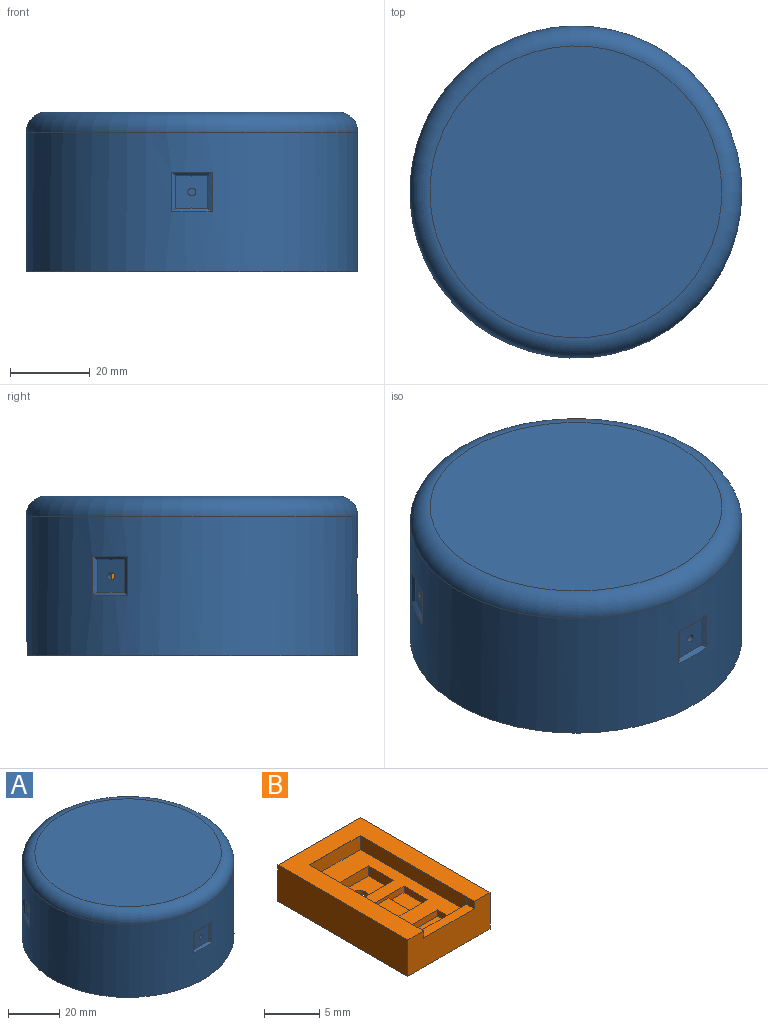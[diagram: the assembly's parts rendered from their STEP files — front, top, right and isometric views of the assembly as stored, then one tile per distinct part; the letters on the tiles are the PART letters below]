
ASSEMBLY  parts=2 mates=1
PART A: 57 faces, bbox 90.2x90.2x40.3 mm
  f0: cylinder r=41.5mm len=83mm, axis (0,0,1), area 8782.8mm2, adj f1,f21,f40,f41,f42,f43,f44,f45
  f1: plane 83x82.62mm, normal (0,0,-1), area 367.1mm2, adj f0,f16,f52,f53
  f2: cylinder r=1mm len=2.48mm, axis (-0.87,-0.5,0), area 9.4mm2, adj f35,f38
  f3: plane 10.81x7.97mm, normal (0,0,-1), area 32.2mm2, adj f4,f6,f32,f36
  f4: plane 16.85x2.6mm, normal (-0.5,-0.87,0), area 50.5mm2, adj f3,f5,f32,f36
  f5: plane 10.81x7.97mm, normal (0,0,1), area 32.2mm2, adj f4,f6,f32,f36
  f6: plane 16.85x2.6mm, normal (0.5,0.87,0), area 50.5mm2, adj f3,f5,f32,f36
  f7: plane 10.81x7.97mm, normal (0,0,-1), area 32.2mm2, adj f8,f10,f28,f35
  f8: plane 16.85x2.6mm, normal (0.5,-0.87,0), area 50.5mm2, adj f7,f9,f28,f35
  f9: plane 10.81x7.97mm, normal (0,0,1), area 32.2mm2, adj f8,f10,f28,f35
  f10: plane 16.85x2.6mm, normal (-0.5,0.87,0), area 50.5mm2, adj f7,f9,f28,f35
  f11: plane 10.75x3mm, normal (0,0,-1), area 32.2mm2, adj f12,f14,f24,f34
  f12: plane 16.85x3mm, normal (1,0,0), area 50.5mm2, adj f11,f13,f24,f34
  f13: plane 10.75x3mm, normal (0,0,1), area 32.2mm2, adj f12,f14,f24,f34
  f14: plane 16.85x3mm, normal (-1,0,0), area 50.5mm2, adj f11,f13,f24,f34
  f15: cylinder r=1mm len=2.48mm, axis (0.87,-0.5,0), area 9.4mm2, adj f36,f39
  f16: cylinder r=40mm len=80mm, axis (0,0,1), area 7542.1mm2, adj f1,f20,f22,f23,f25,f26,f27,f29
  f17: cylinder r=1mm len=2mm, axis (0,1,0), area 9.4mm2, adj f34,f37
  f18: plane 73x73mm, normal (0,0,1), area 4185.4mm2, adj f21
  f19: plane 70x70mm, normal (0,0,-1), area 3848.5mm2, adj f20
  f20: torus R=35mm, axis (0,0,1), area 1605.9mm2, adj f16,f19,f22,f23,f24,f26,f27,f28
  f21: torus R=36.5mm, axis (0,0,1), area 1958.3mm2, adj f0,f18
  f22: plane 25.26x3.71mm, normal (-1,0,0), area 80.6mm2, adj f16,f20,f24,f25
  f23: plane 25.26x3.71mm, normal (1,0,0), area 80.6mm2, adj f16,f20,f24,f25
  f24: plane 25.14x13.75mm, normal (0,1,0), area 163.8mm2, adj f11,f12,f13,f14,f20,f22,f23,f25
  f25: plane 13.75x4mm, normal (0,0,-1), area 52.3mm2, adj f16,f22,f23,f24
  f26: plane 25.26x3.25mm, normal (0.5,-0.87,0), area 80.6mm2, adj f16,f20,f28,f29
  f27: plane 25.26x3.25mm, normal (-0.5,0.87,0), area 80.6mm2, adj f16,f20,f28,f29
  f28: plane 25.14x11.91mm, normal (-0.87,-0.5,0), area 163.8mm2, adj f7,f8,f9,f10,f20,f26,f27,f29
  f29: plane 13.61x9.82mm, normal (0,0,-1), area 52.3mm2, adj f16,f26,f27,f28
  f30: plane 25.26x3.25mm, normal (0.5,0.87,0), area 80.6mm2, adj f16,f20,f32,f33
  f31: plane 25.26x3.25mm, normal (-0.5,-0.87,0), area 80.6mm2, adj f16,f20,f32,f33
  f32: plane 25.14x11.91mm, normal (0.87,-0.5,0), area 163.8mm2, adj f3,f4,f5,f6,f20,f30,f31,f33
  f33: plane 13.61x9.82mm, normal (0,0,-1), area 52.3mm2, adj f16,f30,f31,f32
  f34: plane 16.85x10.75mm, normal (0,1,0), area 178mm2, adj f11,f12,f13,f14,f17
  f35: plane 16.85x9.31mm, normal (-0.87,-0.5,0), area 178mm2, adj f2,f7,f8,f9,f10
  f36: plane 16.85x9.31mm, normal (0.87,-0.5,0), area 178mm2, adj f3,f4,f5,f6,f15
  f37: plane 8.57x8.32mm, normal (0,-1,0), area 61.4mm2, adj f17,f48,f49,f50,f51
  f38: plane 8.57x7.24mm, normal (0.87,0.5,0), area 61.4mm2, adj f2,f44,f45,f46,f47
  f39: plane 8.57x7.24mm, normal (-0.87,0.5,0), area 61.4mm2, adj f15,f40,f41,f42,f43
  f40: bspline ~10.67x1.28mm, area 11.7mm2, adj f0,f39,f41,f42
  f41: bspline ~9.51x6.07mm, area 11.8mm2, adj f0,f39,f40,f43
  f42: bspline ~9.51x6.07mm, area 11.8mm2, adj f0,f39,f40,f43
  f43: bspline ~10.67x1.13mm, area 11.7mm2, adj f0,f39,f41,f42
  f44: bspline ~10.67x1.28mm, area 11.7mm2, adj f0,f38,f45,f46
  f45: bspline ~9.51x6.07mm, area 11.8mm2, adj f0,f38,f44,f47
  f46: bspline ~9.51x6.07mm, area 11.8mm2, adj f0,f38,f44,f47
  f47: bspline ~10.67x1.13mm, area 11.7mm2, adj f0,f38,f45,f46
  f48: bspline ~10.67x1.08mm, area 11.7mm2, adj f0,f37,f49,f50
  f49: bspline ~10.54x1.44mm, area 11.8mm2, adj f0,f37,f48,f51
  f50: bspline ~10.54x1.44mm, area 11.8mm2, adj f0,f37,f48,f51
  f51: bspline ~10.67x1.08mm, area 11.7mm2, adj f0,f37,f49,f50
  f52: plane 1.85x1.51mm, normal (-1,0,0), area 2.8mm2, adj f0,f1,f16,f56
  f53: plane 1.85x1.51mm, normal (1,0,0), area 2.8mm2, adj f0,f1,f16,f55
  f54: plane 7.55x1.68mm, normal (0,0,-1), area 11.3mm2, adj f0,f16,f55,f56
  f55: cylinder r=1.85mm len=1.85mm, axis (0,1,0), area 4.4mm2, adj f0,f16,f53,f54
  f56: cylinder r=1.85mm len=1.85mm, axis (0,-1,0), area 4.4mm2, adj f0,f16,f52,f54
PART B: 38 faces, bbox 10.6x16.7x4.1 mm
  f0: plane 3x2mm, normal (0,0,1), area 6mm2, adj f1,f12,f13,f36
  f1: plane 6x1.1mm, normal (0,-1,0), area 4.2mm2, adj f0,f2,f11,f12,f14,f35,f36,f37
  f2: plane 3x2mm, normal (0,0,1), area 6mm2, adj f1,f11,f13,f35
  f3: plane 3.2x1.1mm, normal (1,0,0), area 3.5mm2, adj f8,f10,f14,f33
  f4: plane 14.58x0.02mm, normal (0,0,-1), area 0.3mm2, adj f16,f29
  f5: plane 3x0.7mm, normal (1,0,0), area 2.1mm2, adj f6,f14,f19,f34
  f6: plane 5x0.7mm, normal (0,-1,0), area 3.5mm2, adj f5,f7,f14,f34
  f7: plane 3x0.7mm, normal (-1,0,0), area 2.1mm2, adj f6,f14,f19,f34
  f8: plane 4x1.1mm, normal (0,-1,0), area 4.4mm2, adj f3,f9,f14,f33
  f9: plane 3.2x1.1mm, normal (-1,0,0), area 3.5mm2, adj f8,f10,f14,f33
  f10: plane 4x1.1mm, normal (0,1,0), area 4.4mm2, adj f3,f9,f14,f33
  f11: plane 3x1.1mm, normal (1,0,0), area 3.3mm2, adj f1,f2,f13,f14
  f12: plane 3x0.7mm, normal (-1,0,0), area 2.1mm2, adj f0,f1,f13,f14
  f13: plane 6x1.1mm, normal (0,1,0), area 4.2mm2, adj f0,f2,f11,f12,f14,f35,f36,f37
  f14: plane 14.6x8.5mm, normal (0,0,1), area 78.3mm2, adj f1,f3,f5,f6,f7,f8,f9,f10
  f15: plane 16.6x10.5mm, normal (0,0,-1), area 171.2mm2, adj f20,f21,f22,f23,f32
  f16: plane 14.6x1.75mm, normal (-1,0,0), area 25.5mm2, adj f4,f14,f17,f19
  f17: plane 8.5x1.75mm, normal (0,-1,0), area 14.9mm2, adj f14,f16,f18,f25
  f18: plane 14.6x1.75mm, normal (1,0,0), area 25.5mm2, adj f14,f17,f19,f25
  f19: plane 8.56x3.31mm, normal (0,1,0), area 19mm2, adj f5,f7,f14,f16,f18,f24,f26,f27
  f20: plane 10.5x4.05mm, normal (0,1,0), area 42.5mm2, adj f15,f21,f23,f28
  f21: plane 16.6x4.05mm, normal (1,0,0), area 67.2mm2, adj f15,f20,f22,f28
  f22: plane 10.5x4.05mm, normal (0,-1,0), area 37.3mm2, adj f15,f21,f23,f24,f26,f27,f28
  f23: plane 16.6x4.05mm, normal (-1,0,0), area 67.2mm2, adj f15,f20,f22,f28
  f24: plane 6.5x1mm, normal (0,0,1), area 6.5mm2, adj f19,f22,f26,f27
  f25: plane 14.6x8.48mm, normal (0,0,-1), area 0.3mm2, adj f17,f18,f30,f31
  f26: plane 1x0.8mm, normal (1,0,0), area 0.8mm2, adj f19,f22,f24,f28
  f27: plane 1x0.8mm, normal (-1,0,0), area 0.8mm2, adj f19,f22,f24,f28
  f28: plane 16.6x10.5mm, normal (0,0,1), area 79.4mm2, adj f20,f21,f22,f23,f26,f27,f29,f30
  f29: bspline ~15.26x0.98mm, area 18mm2, adj f4,f19,f28,f31
  f30: bspline ~15.26x0.98mm, area 18mm2, adj f19,f25,f28,f31
  f31: bspline ~8.74x0.98mm, area 9.5mm2, adj f25,f28,f29,f30
  f32: cylinder r=1mm len=2mm, axis (0,0,-1), area 2.5mm2, adj f15,f33
  f33: plane 4x3.2mm, normal (0,0,1), area 9.7mm2, adj f3,f8,f9,f10,f32
  f34: plane 5x3mm, normal (0,0,1), area 15mm2, adj f5,f6,f7,f19
  f35: plane 3x0.8mm, normal (-1,0,0), area 2.4mm2, adj f1,f2,f13,f37
  f36: plane 3x0.4mm, normal (1,0,0), area 1.2mm2, adj f0,f1,f13,f37
  f37: plane 3x2mm, normal (0,0,1), area 6mm2, adj f1,f13,f35,f36
PLACE A at identity
PLACE B rot(axis=(0.77,-0.45,-0.45),104.5deg) t=(22.84,38.44,-16.69)mm
MATE fastened B.f15 <-> A.f35  axis (0.87,0.5,0) through (36.46,14.85,-8.39)mm
